# Revit family: Overhead_Door-CHI-LiftReady
name_source: partatom
category: Specialty Equipment
units: mm (PartAtom-declared; Revit-internal decimal feet)

## family parameters
Always vertical = Yes
Cut with Voids When Loaded = No
Enable Cutting in Views = No
Host = Wall
Maintain Annotation Orientation = No
OmniClass Number = 23.30.10.21
OmniClass Title = Special Function Doors
Part Type = Normal
Room Calculation Point = No
Round Connector Dimension = Use Diameter
Shared = No

## types (1)
- Not a Type - Load Type Catalog
    Assembly Code = B2030410
    C Ceiling Upset = 6 "
    C Endplate Depth = 15 "
    C Endplate Height = 15 "
    C Side Overlap = 1.5 "
    C Side Width = 3 "
    Default Elevation = 0 "
    Description = Lift Ready Series
    Keynote = 08110
    Labyrinth = No
    Manufacturer = C.H.I. Overhead Doors
    Manufacturer Fax Number = 800-677-2650
    Material = Steel - C.H.I Overhead Doors - Clear
    Model = Portcullis
    Portcullis = Yes
    Product Documentation Link = Contact Manufacturer for More Information
    Product Page URL = Contact Manufacturer for More Information
    URL = https://www.chiohd.com
    Version = 2021-v1.a
    Warranty URL = https://www.chiohd.com

## geometry (parser evidence)
native form markers: Sweep x19
no freeform markers — native parametric forms only
